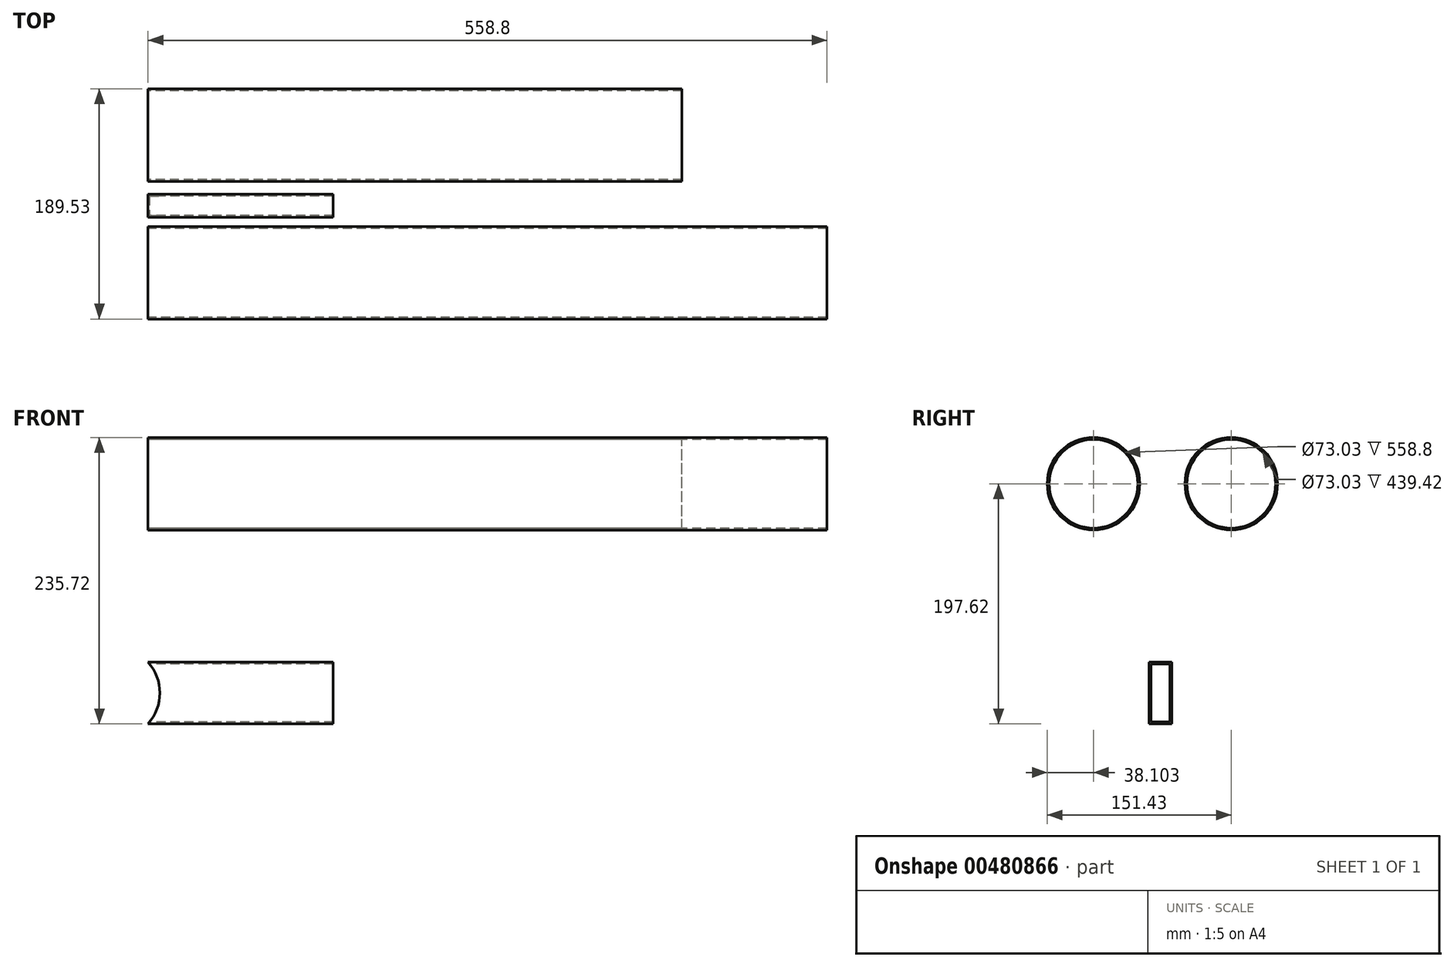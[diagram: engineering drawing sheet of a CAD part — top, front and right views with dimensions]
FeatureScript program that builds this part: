
annotation { "Feature Type Name" : "Feature", "Feature Type Description" : "" }
export const myFeature = defineFeature(function(context is Context, id is Id, definition is map)
    precondition{}
    {
        {
            var Q0;
            Q0=qCreatedBy(makeId("Right.planeOp"),FACE);
            var sketch = newSketch(context, id + "F0", { "sketchPlane" : qUnion([Q0])});
            skCircle(sketch, "E0", {"center": v(0, 0) * mm, "radius": 38.1 * mm});
            skCircle(sketch, "E1", {"center": v(0, 0) * mm, "radius": 36.51 * mm});
            skSolve(sketch);
        }
        {
            var Q0;
            Q0 = qSketchRegion(id + "F0", true);
            var Q1;
            Q1=makeQuery(id+"F0.imprint","IMPRINT",FACE,{"disambiguationData":[TD([[makeQuery(id+"F0.imprint","IMPRINT",EDGE,{"derivedFrom":sQuery(id+"F0.wireOp",EDGE,"E0")}),1.0]])]});
            extrude(context, id + "F1", {"entities" : qUnion([Q0, Q1]), "depth" : 439.42 * mm});
        }
        {
            var Q0;
            Q0=qCreatedBy(makeId("Right.planeOp"),FACE);
            var sketch = newSketch(context, id + "F2", { "sketchPlane" : qUnion([Q0])});
            skCircle(sketch, "E2", {"center": v(-113.33, 0) * mm, "radius": 38.1 * mm});
            skCircle(sketch, "E3", {"center": v(-113.33, 0) * mm, "radius": 36.51 * mm});
            skSolve(sketch);
        }
        {
            var Q0;
            Q0=makeQuery(id+"F2.imprint","IMPRINT",FACE,{"disambiguationData":[TD([[makeQuery(id+"F2.imprint","IMPRINT",EDGE,{"derivedFrom":sQuery(id+"F2.wireOp",EDGE,"E2")}),1.0]])]});
            extrude(context, id + "F3", {"entities" : qUnion([Q0]), "depth" : 558.8 * mm});
        }
        {
            var Q0;
            Q0=qCreatedBy(makeId("Right.planeOp"),FACE);
            var sketch = newSketch(context, id + "F4", { "sketchPlane" : qUnion([Q0])});
            skLineSegment(sketch, "E4.bottom", {"start": v(-67.7, -146.82) * mm, "end": v(-48.74, -146.82) * mm});
            skLineSegment(sketch, "E4.top", {"start": v(-67.7, -197.62) * mm, "end": v(-48.74, -197.62) * mm});
            skLineSegment(sketch, "E4.left", {"start": v(-67.7, -146.82) * mm, "end": v(-67.7, -197.62) * mm});
            skLineSegment(sketch, "E4.right", {"start": v(-48.74, -146.82) * mm, "end": v(-48.74, -197.62) * mm});
            skLineSegment(sketch, "E5.0", {"start": v(-66.1, -148.4) * mm, "end": v(-50.33, -148.4) * mm});
            skLineSegment(sketch, "E5.1", {"start": v(-66.1, -148.4) * mm, "end": v(-66.1, -196.03) * mm});
            skLineSegment(sketch, "E5.2", {"start": v(-66.1, -196.03) * mm, "end": v(-50.33, -196.03) * mm});
            skLineSegment(sketch, "E6.0", {"start": v(-50.33, -148.4) * mm, "end": v(-50.33, -196.03) * mm});
            skSolve(sketch);
        }
        {
            var Q0;
            Q0=makeQuery(id+"F4.imprint","IMPRINT",FACE,{"disambiguationData":[TD([[makeQuery(id+"F4.imprint","IMPRINT",EDGE,{"derivedFrom":sQuery(id+"F4.wireOp",EDGE,"E4.bottom")}),-1.0]])]});
            extrude(context, id + "F5", {"entities" : qUnion([Q0]), "depth" : 152.4 * mm});
        }
        {
            var Q0;
            Q0=makeQuery(id+"F5.opExtrude","SWEPT_FACE",FACE,{"disambiguationData":[OSD([sQuery(id+"F4.wireOp",EDGE,"E4.left")])]});
            var sketch = newSketch(context, id + "F6", { "sketchPlane" : qUnion([Q0])});
            skArc(sketch, "E7", {"start": v(0, -197.62) * mm, "mid": v(9.7, -172.22) * mm, "end": v(0, -146.82) * mm});
            skSolve(sketch);
        }
        {
            var Q0;
            Q0=makeQuery(id+"F6.imprint","IMPRINT",FACE,{"disambiguationData":[TD([[makeQuery(id+"F6.imprint","IMPRINT",EDGE,{"derivedFrom":sQuery(id+"F6.wireOp",EDGE,"E7")}),1.0]])]});
            extrude(context, id + "F7", {"entities" : qUnion([Q0]), "operationType" : NewBodyOperationType.REMOVE, "oppositeDirection" : true, "depth" : 50.8 * mm});
        }
    });
